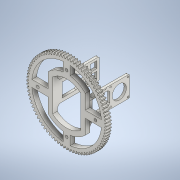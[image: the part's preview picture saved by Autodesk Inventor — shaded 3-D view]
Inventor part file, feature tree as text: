
AUTODESK INVENTOR PART (.ipt)
format: ipt  version: 2020 (Build 240168000, 168)  size: 770,560 bytes
history: native  units: mm (DEFAULTED — no unit token found)
features: extrude x12, sketch x12, plane x4, projected_geometry x4, other x3, fillet x1, chamfer x1
ambient origin geometry x8: Origin, YZ Plane, XZ Plane, XY Plane, X Axis, Y Axis, Z Axis, Center Point
bodies: Solid1 (feature_tree)
feature tree (37):
  extrude  "Extrusion1"  Depth=12.7mm TaperAngle=0.0deg
  plane  "Work Plane1"
  plane  "Work Plane2"
  plane  "Work Plane3"
  other  "Spur Gear"
  extrude  "Extrusion8"  Depth=76.2mm TaperAngle=0.0deg
  sketch  "Sketch9"  dims[d14=0.0mm d15=124.46mm d16=0.0mm]
  extrude  "Extrusion9"  TaperAngle=0.0deg  [1 undecoded]
  extrude  "Extrusion10"  TaperAngle=0.0deg  [1 undecoded]
  extrude  "Extrusion11"  Depth=6.35mm
  extrude  "Extrusion12"  Depth=146.05mm
  fillet  "Fillet3"  Radius=7.62mm
  extrude  "Extrusion13"  Depth=1.8288mm
  extrude  "Extrusion14"  Depth=25.4mm TaperAngle=0.0deg
  extrude  "Extrusion15"  Depth=6.35mm
  chamfer  "Chamfer2"  Distance=25.4mm
  extrude  "Extrusion17"  Depth=56.4mm
  extrude  "Extrusion18"  Depth=12.7mm
  plane  "Work Plane5"
  extrude  "Extrusion19"  Depth=12.7mm
  sketch  "Sketch1"  dims[d0=218.44mm d1=12.7mm d2=0.0mm]
  sketch  "Sketch2"  dims[d3=213.36mm d4=76.2mm d5=0.0mm]
  other  "Srf1"
  sketch  "Sketch3"  dims[d6=0.0mm d7=0.373999mm d9=0.0mm]
  sketch  "Sketch10"  dims[d17=0.0mm d18=0.0mm d19=124.46mm d47=6.35mm d48=6.35mm]
  sketch  "Sketch11"  dims[d66=116.205mm d67=146.05mm d68=7.62mm]
  sketch  "Sketch12"  dims[d69=7.62mm d70=1.8288mm]
  sketch  "Sketch15"  dims[d71=1.8288mm d72=25.4mm d73=0.0mm]
  projected_geometry  "Projected Loop1"
  projected_geometry  "Projected Loop2"
  sketch  "Sketch16"  dims[d75=56.4mm d76=6.35mm]
  sketch  "Sketch17"  dims[d77=76.2mm d78=25.4mm d79=0.0mm]
  projected_geometry  "Projected Loop3"
  sketch  "Sketch18"  dims[d80=127.0mm d81=0.0mm d82=56.4mm]
  projected_geometry  "Projected Loop4"
  sketch  "Sketch20"  dims[d83=4.5mm d85=47.14mm d86=38.6mm d87=127.0mm d88=0.0mm d89=56.4mm d90=5.207mm d91=127.0mm d92=0.0mm d93=3.175mm d97=12.7mm d98=19.05mm d99=12.7mm d100=19.05mm d101=127.0mm d102=0.0mm d103=6.35mm d104=50.8mm d105=6.35mm d106=127.0mm d107=0.0mm d108=127.0mm d109=0.0mm d110=6.35mm d111=3.175mm d112=45.0deg d113=6.35mm d114=6.35mm d115=6.35mm d116=6.35mm d119=3.175mm d120=3.175mm d121=25.4mm d122=0.0mm d123=6.35mm d124=6.35mm d125=6.35mm d126=135.0deg d127=135.0deg d128=25.4mm d129=0.0mm d130=7.62mm d131=157.3276mm d132=78.6638mm d133=25.4mm d134=0.0mm d74=12.7mm]
  other  "Pitch Diameter"
note: 2 required parameter values undecoded (feature->parameter linkage not recoverable at this tier; creation-order binding heuristic only, values carry confidence <= 0.55)
